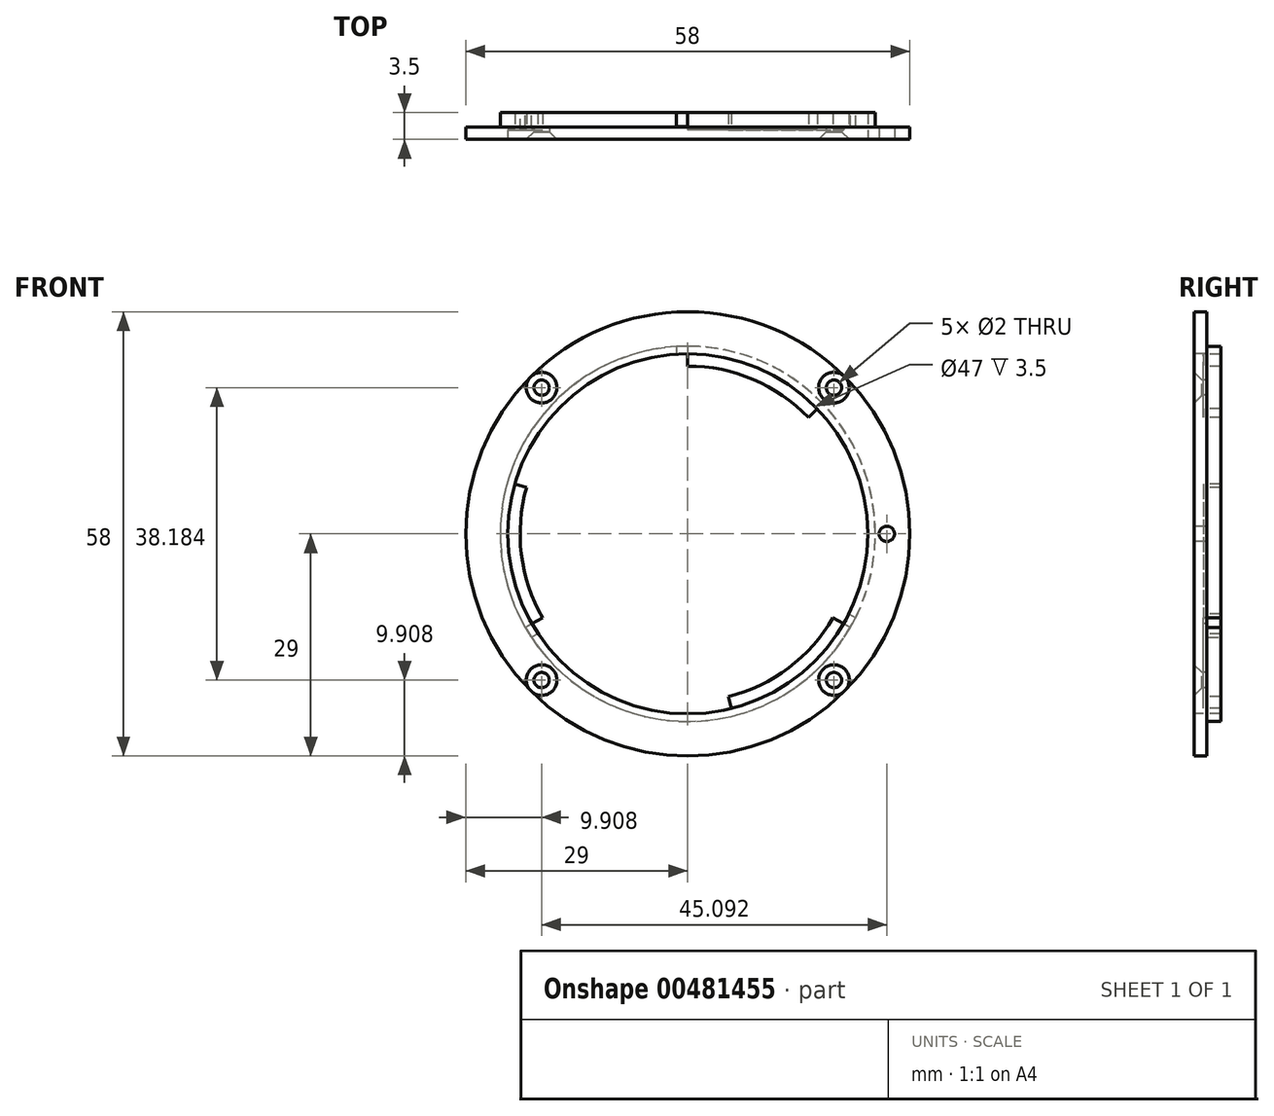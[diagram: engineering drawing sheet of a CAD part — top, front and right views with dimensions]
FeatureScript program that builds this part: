
annotation { "Feature Type Name" : "Feature", "Feature Type Description" : "" }
export const myFeature = defineFeature(function(context is Context, id is Id, definition is map)
    precondition{}
    {
        {
            var Q0;
            Q0=qCreatedBy(makeId("Front.planeOp"),FACE);
            var sketch = newSketch(context, id + "F0", { "sketchPlane" : qUnion([Q0])});
            skCircle(sketch, "E0", {"center": v(0, 0) * mm, "radius": 29 * mm});
            skCircle(sketch, "E1", {"center": v(0, 0) * mm, "radius": 21.9 * mm});
            skSolve(sketch);
        }
        {
            var Q0;
            Q0 = qSketchRegion(id + "F0", true);
            extrude(context, id + "F1", {"entities" : qUnion([Q0]), "depth" : 3.5 * mm});
        }
        {
            var Q0;
            Q0=makeQuery(id+"F1.opExtrude","CAP_FACE",FACE,{"disambiguationData":[OSD([sQuery(id+"F0.wireOp",EDGE,"E0"),sQuery(id+"F0.wireOp",EDGE,"E1")])],"isStart":false});
            var sketch = newSketch(context, id + "F2", { "sketchPlane" : qUnion([Q0])});
            skCircle(sketch, "E2", {"center": v(0, 0) * mm, "radius": 23.5 * mm});
            skSolve(sketch);
        }
        {
            var Q0;
            Q0 = qSketchRegion(id + "F2", true);
            extrude(context, id + "F3", {"entities" : qUnion([Q0]), "operationType" : NewBodyOperationType.REMOVE, "oppositeDirection" : true, "depth" : 1.2 * mm});
        }
        {
            var Q0;
            Q0=makeQuery(id+"F1.opExtrude","CAP_FACE",FACE,{"disambiguationData":[OSD([sQuery(id+"F0.wireOp",EDGE,"E0"),sQuery(id+"F0.wireOp",EDGE,"E1")])],"isStart":false});
            var sketch = newSketch(context, id + "F4", { "sketchPlane" : qUnion([Q0])});
            skArc(sketch, "E3", {"start": v(0, 23.5) * mm, "mid": v(-14.14, 18.77) * mm, "end": v(-22.59, 6.48) * mm});
            skArc(sketch, "E4", {"start": v(5.3, -21.25) * mm, "mid": v(13.18, -17.5) * mm, "end": v(18.97, -10.95) * mm});
            skLineSegment(sketch, "E5", {"start": v(0, 23.5) * mm, "end": v(0, 21.9) * mm});
            skLineSegment(sketch, "E6", {"start": v(-20.35, -11.75) * mm, "end": v(-18.97, -10.95) * mm});
            skLineSegment(sketch, "E7", {"start": v(20.35, -11.75) * mm, "end": v(18.97, -10.95) * mm});
            skLineSegment(sketch, "E8", {"start": v(16.9, 16.32) * mm, "end": v(15.75, 15.21) * mm});
            skLineSegment(sketch, "E9", {"start": v(-22.59, 6.48) * mm, "end": v(-21.05, 6.04) * mm});
            skLineSegment(sketch, "E10", {"start": v(5.69, -22.8) * mm, "end": v(5.3, -21.25) * mm});
            skArc(sketch, "E11.trimOffspring", {"start": v(-20.35, -11.75) * mm, "mid": v(-9.18, -21.63) * mm, "end": v(5.69, -22.8) * mm});
            skArc(sketch, "E12.trimOffspring", {"start": v(20.35, -11.75) * mm, "mid": v(23.32, 2.86) * mm, "end": v(16.9, 16.32) * mm});
            skArc(sketch, "E13.trimOffspring", {"start": v(-21.05, 6.04) * mm, "mid": v(-21.74, -2.67) * mm, "end": v(-18.97, -10.95) * mm});
            skArc(sketch, "E14.trimOffspring", {"start": v(15.75, 15.21) * mm, "mid": v(8.56, 20.16) * mm, "end": v(0, 21.9) * mm});
            skPoint(sketch, "E15.orphan", {"position": v(0, 31.34) * mm});
            skSolve(sketch);
        }
        {
            var Q0;
            Q0 = qSketchRegion(id + "F4", true);
            extrude(context, id + "F5", {"entities" : qUnion([Q0]), "operationType" : NewBodyOperationType.REMOVE, "endBound" : BoundingType.THROUGH_ALL, "oppositeDirection" : true, "depth" : 25 * mm});
        }
        {
            var Q0;
            Q0=makeQuery(id+"F1.opExtrude","CAP_FACE",FACE,{"disambiguationData":[OSD([sQuery(id+"F0.wireOp",EDGE,"E0"),sQuery(id+"F0.wireOp",EDGE,"E1")])],"isStart":true});
            var sketch = newSketch(context, id + "F6", { "sketchPlane" : qUnion([Q0])});
            skCircle(sketch, "E16", {"center": v(0, 0) * mm, "radius": 24.5 * mm});
            skCircle(sketch, "E17", {"center": v(0, 0) * mm, "radius": 30.5 * mm});
            skSolve(sketch);
        }
        {
            var Q0;
            Q0 = qSketchRegion(id + "F6", true);
            extrude(context, id + "F7", {"entities" : qUnion([Q0]), "operationType" : NewBodyOperationType.REMOVE, "oppositeDirection" : true, "depth" : 1.9 * mm});
        }
        {
            var Q0;
            Q0=makeQuery(id+"F1.opExtrude","CAP_FACE",FACE,{"disambiguationData":[OSD([sQuery(id+"F0.wireOp",EDGE,"E0"),sQuery(id+"F0.wireOp",EDGE,"E1")])],"isStart":true});
            var sketch = newSketch(context, id + "F8", { "sketchPlane" : qUnion([Q0])});
            skLineSegment(sketch, "E18.bottom", {"start": v(0, 0) * mm, "end": v(-0.75, -1.3) * mm});
            skLineSegment(sketch, "E18.top", {"start": v(21.65, -12.5) * mm, "end": v(20.9, -13.8) * mm});
            skLineSegment(sketch, "E18.left", {"start": v(0, 0) * mm, "end": v(21.65, -12.5) * mm});
            skLineSegment(sketch, "E18.right", {"start": v(-0.75, -1.3) * mm, "end": v(20.9, -13.8) * mm});
            skLineSegment(sketch, "E19.bottom", {"start": v(1.5, 25) * mm, "end": v(0, 25) * mm});
            skLineSegment(sketch, "E19.top", {"start": v(1.5, 0) * mm, "end": v(0, 0) * mm});
            skLineSegment(sketch, "E19.left", {"start": v(1.5, 25) * mm, "end": v(1.5, 0) * mm});
            skLineSegment(sketch, "E19.right", {"start": v(0, 25) * mm, "end": v(0, 0) * mm});
            skLineSegment(sketch, "E20.bottom", {"start": v(0, 0) * mm, "end": v(-0.75, 1.3) * mm});
            skLineSegment(sketch, "E20.top", {"start": v(-21.65, -12.5) * mm, "end": v(-22.4, -11.2) * mm});
            skLineSegment(sketch, "E20.left", {"start": v(0, 0) * mm, "end": v(-21.65, -12.5) * mm});
            skLineSegment(sketch, "E20.right", {"start": v(-0.75, 1.3) * mm, "end": v(-22.4, -11.2) * mm});
            skSolve(sketch);
        }
        {
            var Q0;
            Q0 = qSketchRegion(id + "F8", true);
            extrude(context, id + "F9", {"entities" : qUnion([Q0]), "operationType" : NewBodyOperationType.REMOVE, "oppositeDirection" : true, "depth" : 1.85 * mm});
        }
        {
            var Q0;
            Q0=makeQuery(id+"F1.opExtrude","CAP_FACE",FACE,{"disambiguationData":[OSD([sQuery(id+"F0.wireOp",EDGE,"E0"),sQuery(id+"F0.wireOp",EDGE,"E1")])],"isStart":false});
            var sketch = newSketch(context, id + "F10", { "sketchPlane" : qUnion([Q0])});
            skPoint(sketch, "E21", {"position": v(26, 0) * mm});
            skSolve(sketch);
        }
        {
            var Q0;
            Q0=sQuery(id+"F10.wireOp",VERTEX,"E21");
            var Q1;
            Q1=makeQuery(id+"F1.opExtrude","SWEPT_BODY",BODY,{"disambiguationData":[OSD([sQuery(id+"F0.wireOp",EDGE,"E0"),sQuery(id+"F0.wireOp",EDGE,"E1")])]});
            hole(context, id + "F11", {"style" : HoleStyle.SIMPLE, "endStyle" : HoleEndStyle.THROUGH, "holeDiameter" : 2 * mm, "isTappedThrough" : true, "tappedDepth" : 12 * mm, "tapClearance" : 3, "locations" : qUnion([Q0]), "scope" : qUnion([Q1])});
        }
        {
            var Q0;
            Q0=makeQuery(id+"F1.opExtrude","CAP_FACE",FACE,{"disambiguationData":[OSD([sQuery(id+"F0.wireOp",EDGE,"E0"),sQuery(id+"F0.wireOp",EDGE,"E1")])],"isStart":false});
            var sketch = newSketch(context, id + "F12", { "sketchPlane" : qUnion([Q0])});
            skCircle(sketch, "E22", {"center": v(0, 0) * mm, "radius": 27 * mm, "construction": true});
            skLineSegment(sketch, "E23", {"start": v(0, 0) * mm, "end": v(33.94, 33.94) * mm, "construction": true});
            skLineSegment(sketch, "E24", {"start": v(-28.67, 28.67) * mm, "end": v(0, 0) * mm, "construction": true});
            skLineSegment(sketch, "E25", {"start": v(-32.27, -32.27) * mm, "end": v(0, 0) * mm, "construction": true});
            skLineSegment(sketch, "E26", {"start": v(30.8, -30.8) * mm, "end": v(0, 0) * mm, "construction": true});
            skPoint(sketch, "E27", {"position": v(-19.1, 19.1) * mm});
            skPoint(sketch, "E28", {"position": v(19.1, 19.1) * mm});
            skPoint(sketch, "E29", {"position": v(19.1, -19.1) * mm});
            skPoint(sketch, "E30", {"position": v(-19.1, -19.1) * mm});
            skSolve(sketch);
        }
        {
            var Q0;
            Q0=sQuery(id+"F12.wireOp",VERTEX,"E27");
            var Q1;
            Q1=sQuery(id+"F12.wireOp",VERTEX,"E28");
            var Q2;
            Q2=sQuery(id+"F12.wireOp",VERTEX,"E29");
            var Q3;
            Q3=sQuery(id+"F12.wireOp",VERTEX,"E30");
            var Q4;
            Q4=makeQuery(id+"F1.opExtrude","SWEPT_BODY",BODY,{"disambiguationData":[OSD([sQuery(id+"F0.wireOp",EDGE,"E0"),sQuery(id+"F0.wireOp",EDGE,"E1")])]});
            hole(context, id + "F13", {"style" : HoleStyle.C_SINK, "endStyle" : HoleEndStyle.BLIND, "holeDiameter" : 2 * mm, "cSinkDiameter" : 4 * mm, "cSinkAngle" : 90 * degree, "holeDepth" : 10 * mm, "isTappedThrough" : true, "tappedDepth" : 12 * mm, "tapClearance" : 3, "locations" : qUnion([Q0, Q1, Q2, Q3]), "scope" : qUnion([Q4])});
        }
    });
